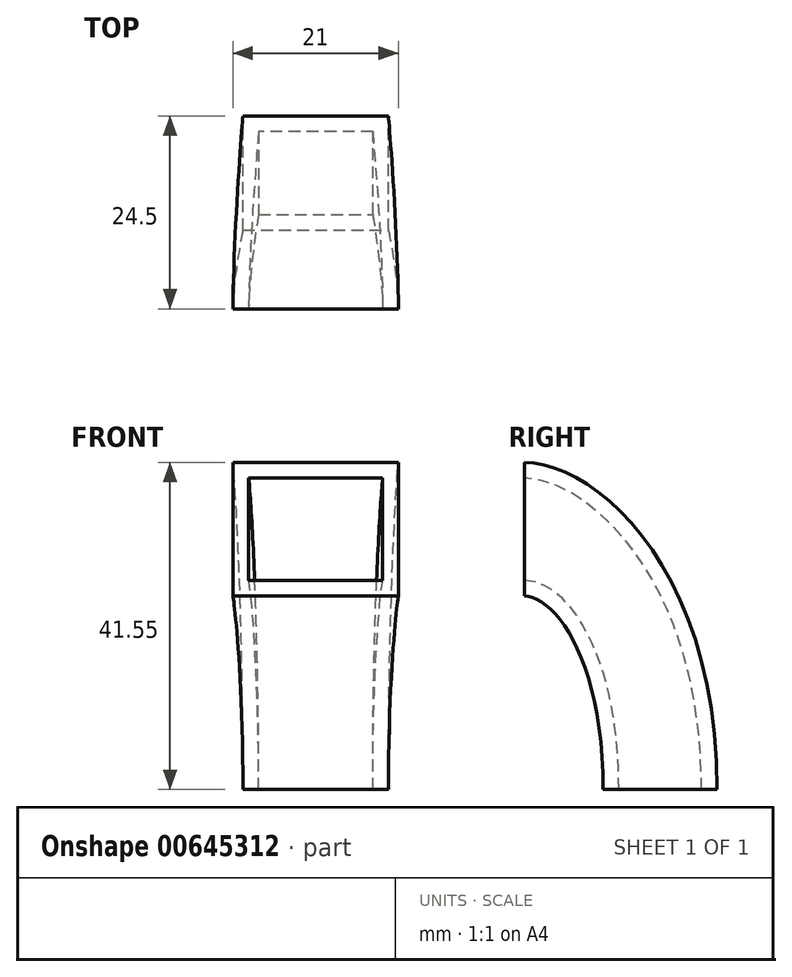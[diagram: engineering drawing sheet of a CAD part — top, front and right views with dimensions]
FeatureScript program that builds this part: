
annotation { "Feature Type Name" : "Feature", "Feature Type Description" : "" }
export const myFeature = defineFeature(function(context is Context, id is Id, definition is map)
    precondition{}
    {
        {
            var Q0;
            Q0=qCreatedBy(makeId("Top.planeOp"),FACE);
            var sketch = newSketch(context, id + "F0", { "sketchPlane" : qUnion([Q0])});
            skLineSegment(sketch, "E0.bottom", {"start": v(0, 0) * mm, "end": v(18.5, 0) * mm});
            skLineSegment(sketch, "E0.top", {"start": v(0, 14.5) * mm, "end": v(18.5, 14.5) * mm});
            skLineSegment(sketch, "E0.left", {"start": v(0, 0) * mm, "end": v(0, 14.5) * mm});
            skLineSegment(sketch, "E0.right", {"start": v(18.5, 0) * mm, "end": v(18.5, 14.5) * mm});
            skSolve(sketch);
        }
        {
            var Q0;
            Q0=qCreatedBy(makeId("Front.planeOp"),FACE);
            cPlane(context, id + "F1", {"entities" : qUnion([Q0]), "cplaneType" : CPlaneType.OFFSET, "offset" : 10 * mm, "width" : 150 * mm, "height" : 150 * mm});
        }
        {
            var Q0;
            Q0=qCreatedBy(id+"F1.planeOp",FACE);
            var sketch = newSketch(context, id + "F2", { "sketchPlane" : qUnion([Q0])});
            skLineSegment(sketch, "E1.top", {"start": v(-1.25, 41.55) * mm, "end": v(19.75, 41.55) * mm});
            skLineSegment(sketch, "E1.left", {"start": v(-1.25, 24.55) * mm, "end": v(-1.25, 41.55) * mm});
            skLineSegment(sketch, "E1.right", {"start": v(19.75, 24.55) * mm, "end": v(19.75, 41.55) * mm});
            skLineSegment(sketch, "E2", {"start": v(19.75, 24.55) * mm, "end": v(-1.25, 24.55) * mm});
            skSolve(sketch);
        }
        {
            var Q0;
            Q0=qCreatedBy(makeId("Right.planeOp"),FACE);
            var sketch = newSketch(context, id + "F3", { "sketchPlane" : qUnion([Q0])});
            skFitSpline(sketch, "E3", {"points": [v(7.2, 0) * mm, v(0.92, 19.28) * mm, v(-10, 33.73) * mm], "startDerivative": vector(-24.65, 44.2) * mm, "endDerivative": vector(-46.86, -1.43) * mm});
            skSolve(sketch);
        }
        {
            var Q0;
            Q0=makeQuery(id+"F0.imprint","IMPRINT",FACE,{"disambiguationData":[TD([[makeQuery(id+"F0.imprint","IMPRINT",EDGE,{"derivedFrom":sQuery(id+"F0.wireOp",EDGE,"E0.bottom")}),1.0]])]});
            var Q1;
            Q1=makeQuery(id+"F2.imprint","IMPRINT",FACE,{"disambiguationData":[TD([[makeQuery(id+"F2.imprint","IMPRINT",EDGE,{"derivedFrom":sQuery(id+"F2.wireOp",EDGE,"E1.top")}),-1.0]])]});
            var Q2;
            Q2=sQuery(id+"F3.wireOp",EDGE,"E3");
            var Q3;
            Q3=sQuery(id+"F0.wireOp",VERTEX,"E0.left.start");
            var Q4;
            Q4=sQuery(id+"F2.wireOp",VERTEX,"E1.left.start");
            loft(context, id + "F4", {"startCondition" : LoftEndDerivativeType.NORMAL_TO_PROFILE, "startMagnitude" : 2, "endCondition" : LoftEndDerivativeType.NORMAL_TO_PROFILE, "endMagnitude" : 1, "sheetProfilesArray" : [{ "sheetProfileEntities" : qUnion([Q0]) }, { "sheetProfileEntities" : qUnion([Q1]) }], "guidesArray" : [{ "guideEntities" : qUnion([Q2]), "guideDerivativeType" : LoftGuideDerivativeType.DEFAULT, "guideDerivativeMagnitude" : 1 }], "matchConnections" : true, "connections" : [{ "connectionEntities" : qUnion([Q3, Q4]), "connectionEdgeQueries" : qUnion([]), "connectionEdgeParameters" : [] }]});
        }
        {
            var Q0;
            Q0=makeQuery(id+"F4.opLoft","CAP_FACE",FACE,{"disambiguationData":[OSD([makeQuery(id+"F2.imprint","IMPRINT",FACE,{"disambiguationData":[TD([[makeQuery(id+"F2.imprint","IMPRINT",EDGE,{"derivedFrom":sQuery(id+"F2.wireOp",EDGE,"E1.top")}),-1.0]])]})])],"isStart":true});
            var Q1;
            Q1=makeQuery(id+"F4.opLoft","CAP_FACE",FACE,{"disambiguationData":[OSD([makeQuery(id+"F0.imprint","IMPRINT",FACE,{"disambiguationData":[TD([[makeQuery(id+"F0.imprint","IMPRINT",EDGE,{"derivedFrom":sQuery(id+"F0.wireOp",EDGE,"E0.bottom")}),1.0]])]})])],"isStart":true});
            shell(context, id + "F5", {"entities" : qUnion([Q0, Q1]), "thickness" : 2 * mm});
        }
    });
